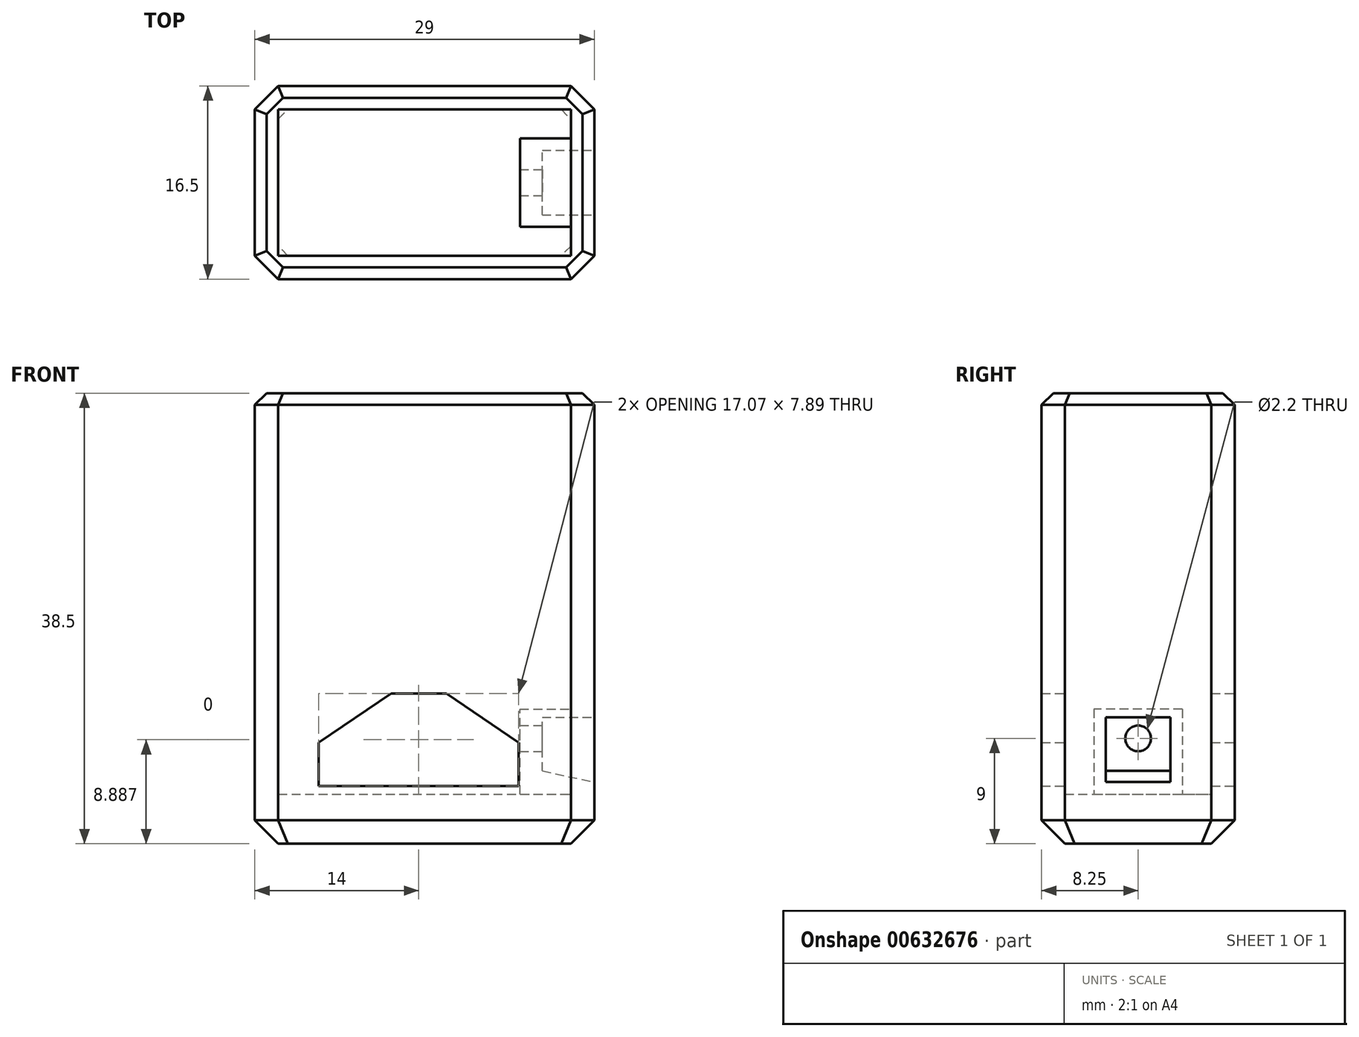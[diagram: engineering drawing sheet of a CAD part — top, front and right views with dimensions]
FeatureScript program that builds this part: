
annotation { "Feature Type Name" : "Feature", "Feature Type Description" : "" }
export const myFeature = defineFeature(function(context is Context, id is Id, definition is map)
    precondition{}
    {
        {
            var Q0;
            Q0=qCreatedBy(makeId("Top.planeOp"),FACE);
            var sketch = newSketch(context, id + "F0", { "sketchPlane" : qUnion([Q0])});
            skLineSegment(sketch, "E0.bottom", {"start": v(0, 0) * mm, "end": v(29, 0) * mm});
            skLineSegment(sketch, "E0.top", {"start": v(0, 16.5) * mm, "end": v(29, 16.5) * mm});
            skLineSegment(sketch, "E0.left", {"start": v(0, 0) * mm, "end": v(0, 16.5) * mm});
            skLineSegment(sketch, "E0.right", {"start": v(29, 0) * mm, "end": v(29, 16.5) * mm});
            skSolve(sketch);
        }
        {
            var Q0;
            Q0=makeQuery(id+"F0.imprint","IMPRINT",FACE,{"disambiguationData":[TD([[makeQuery(id+"F0.imprint","IMPRINT",EDGE,{"derivedFrom":sQuery(id+"F0.wireOp",EDGE,"E0.bottom")}),1.0]])]});
            extrude(context, id + "F1", {"entities" : qUnion([Q0]), "depth" : 38.5 * mm, "offsetDistance" : 25 * mm});
        }
        {
            var Q0;
            Q0=makeQuery(id+"F1.opExtrude","CAP_FACE",FACE,{"disambiguationData":[OSD([sQuery(id+"F0.wireOp",EDGE,"E0.bottom"),sQuery(id+"F0.wireOp",EDGE,"E0.top"),sQuery(id+"F0.wireOp",EDGE,"E0.left"),sQuery(id+"F0.wireOp",EDGE,"E0.right")])],"isStart":false});
            shell(context, id + "F2", {"entities" : qUnion([Q0]), "thickness" : 2 * mm});
        }
        {
            var Q0;
            Q0=makeQuery(id+"F2.opShell","OFFSET_FACE",FACE,{"disambiguationData":[OSD([sQuery(id+"F0.wireOp",EDGE,"E0.bottom"),sQuery(id+"F0.wireOp",EDGE,"E0.top"),sQuery(id+"F0.wireOp",EDGE,"E0.left"),sQuery(id+"F0.wireOp",EDGE,"E0.right")])]});
            extrude(context, id + "F3", {"entities" : qUnion([Q0]), "operationType" : NewBodyOperationType.ADD, "depth" : 2.25 * mm, "offsetDistance" : 25 * mm});
        }
        {
            var Q0;
            Q0=makeQuery(id+"F1.opExtrude","SWEPT_EDGE",EDGE,{"disambiguationData":[OSD([sQuery(id+"F0.wireOp",EDGE,"E0.bottom"),sQuery(id+"F0.wireOp",EDGE,"E0.right")])]});
            var Q1;
            Q1=makeQuery(id+"F1.opExtrude","SWEPT_EDGE",EDGE,{"disambiguationData":[OSD([sQuery(id+"F0.wireOp",EDGE,"E0.top"),sQuery(id+"F0.wireOp",EDGE,"E0.right")])]});
            var Q2;
            Q2=makeQuery(id+"F1.opExtrude","SWEPT_EDGE",EDGE,{"disambiguationData":[OSD([sQuery(id+"F0.wireOp",EDGE,"E0.bottom"),sQuery(id+"F0.wireOp",EDGE,"E0.left")])]});
            var Q3;
            Q3=makeQuery(id+"F1.opExtrude","SWEPT_EDGE",EDGE,{"disambiguationData":[OSD([sQuery(id+"F0.wireOp",EDGE,"E0.top"),sQuery(id+"F0.wireOp",EDGE,"E0.left")])]});
            chamfer(context, id + "F4", {"entities" : qUnion([Q0, Q1, Q2, Q3]), "width" : 2 * mm, "tangentPropagation" : true});
        }
        {
            var Q0;
            Q0=makeQuery(id+"F1.opExtrude","CAP_FACE",FACE,{"disambiguationData":[OSD([sQuery(id+"F0.wireOp",EDGE,"E0.bottom"),sQuery(id+"F0.wireOp",EDGE,"E0.top"),sQuery(id+"F0.wireOp",EDGE,"E0.left"),sQuery(id+"F0.wireOp",EDGE,"E0.right")])],"isStart":true});
            chamfer(context, id + "F5", {"entities" : qUnion([Q0]), "width" : 2 * mm, "tangentPropagation" : true});
        }
        {
            var Q0;
            Q0=makeQuery(id+"F1.opExtrude","CAP_EDGE",EDGE,{"disambiguationData":[OSD([sQuery(id+"F0.wireOp",EDGE,"E0.right")])],"isStart":false});
            var Q1;
            {var subQ0=sQuery(id+"F0.wireOp",EDGE,"E0.right");var subQ1=sQuery(id+"F0.wireOp",EDGE,"E0.bottom");Q1=makeQuery(id+"F4.opChamfer","BLEND_EDGE",EDGE,{"blendedFrom":[makeQuery(id+"F1.opExtrude","SWEPT_EDGE",EDGE,{"disambiguationData":[OSD([subQ1,subQ0])]}),makeQuery(id+"F1.opExtrude","CAP_FACE",FACE,{"disambiguationData":[OSD([subQ1,sQuery(id+"F0.wireOp",EDGE,"E0.top"),sQuery(id+"F0.wireOp",EDGE,"E0.left"),subQ0])],"isStart":false})],"blendedInto":[makeQuery(id+"F1.opExtrude","CAP_FACE",FACE,{"disambiguationData":[OSD([subQ1,sQuery(id+"F0.wireOp",EDGE,"E0.top"),sQuery(id+"F0.wireOp",EDGE,"E0.left"),subQ0])],"isStart":false})]});}
            var Q2;
            Q2=makeQuery(id+"F1.opExtrude","CAP_EDGE",EDGE,{"disambiguationData":[OSD([sQuery(id+"F0.wireOp",EDGE,"E0.bottom")])],"isStart":false});
            var Q3;
            {var subQ0=sQuery(id+"F0.wireOp",EDGE,"E0.left");var subQ1=sQuery(id+"F0.wireOp",EDGE,"E0.bottom");Q3=makeQuery(id+"F4.opChamfer","BLEND_EDGE",EDGE,{"blendedFrom":[makeQuery(id+"F1.opExtrude","SWEPT_EDGE",EDGE,{"disambiguationData":[OSD([subQ1,subQ0])]}),makeQuery(id+"F1.opExtrude","CAP_FACE",FACE,{"disambiguationData":[OSD([subQ1,sQuery(id+"F0.wireOp",EDGE,"E0.top"),subQ0,sQuery(id+"F0.wireOp",EDGE,"E0.right")])],"isStart":false})],"blendedInto":[makeQuery(id+"F1.opExtrude","CAP_FACE",FACE,{"disambiguationData":[OSD([subQ1,sQuery(id+"F0.wireOp",EDGE,"E0.top"),subQ0,sQuery(id+"F0.wireOp",EDGE,"E0.right")])],"isStart":false})]});}
            var Q4;
            Q4=makeQuery(id+"F1.opExtrude","CAP_EDGE",EDGE,{"disambiguationData":[OSD([sQuery(id+"F0.wireOp",EDGE,"E0.left")])],"isStart":false});
            var Q5;
            {var subQ0=sQuery(id+"F0.wireOp",EDGE,"E0.left");var subQ1=sQuery(id+"F0.wireOp",EDGE,"E0.top");Q5=makeQuery(id+"F4.opChamfer","BLEND_EDGE",EDGE,{"blendedFrom":[makeQuery(id+"F1.opExtrude","SWEPT_EDGE",EDGE,{"disambiguationData":[OSD([subQ1,subQ0])]}),makeQuery(id+"F1.opExtrude","CAP_FACE",FACE,{"disambiguationData":[OSD([sQuery(id+"F0.wireOp",EDGE,"E0.bottom"),subQ1,subQ0,sQuery(id+"F0.wireOp",EDGE,"E0.right")])],"isStart":false})],"blendedInto":[makeQuery(id+"F1.opExtrude","CAP_FACE",FACE,{"disambiguationData":[OSD([sQuery(id+"F0.wireOp",EDGE,"E0.bottom"),subQ1,subQ0,sQuery(id+"F0.wireOp",EDGE,"E0.right")])],"isStart":false})]});}
            var Q6;
            Q6=makeQuery(id+"F1.opExtrude","CAP_EDGE",EDGE,{"disambiguationData":[OSD([sQuery(id+"F0.wireOp",EDGE,"E0.top")])],"isStart":false});
            var Q7;
            {var subQ0=sQuery(id+"F0.wireOp",EDGE,"E0.right");var subQ1=sQuery(id+"F0.wireOp",EDGE,"E0.top");Q7=makeQuery(id+"F4.opChamfer","BLEND_EDGE",EDGE,{"blendedFrom":[makeQuery(id+"F1.opExtrude","SWEPT_EDGE",EDGE,{"disambiguationData":[OSD([subQ1,subQ0])]}),makeQuery(id+"F1.opExtrude","CAP_FACE",FACE,{"disambiguationData":[OSD([sQuery(id+"F0.wireOp",EDGE,"E0.bottom"),subQ1,sQuery(id+"F0.wireOp",EDGE,"E0.left"),subQ0])],"isStart":false})],"blendedInto":[makeQuery(id+"F1.opExtrude","CAP_FACE",FACE,{"disambiguationData":[OSD([sQuery(id+"F0.wireOp",EDGE,"E0.bottom"),subQ1,sQuery(id+"F0.wireOp",EDGE,"E0.left"),subQ0])],"isStart":false})]});}
            chamfer(context, id + "F6", {"entities" : qUnion([Q0, Q1, Q2, Q3, Q4, Q5, Q6, Q7]), "width" : 1 * mm, "tangentPropagation" : true});
        }
        {
            var Q0;
            Q0=makeQuery(id+"F1.opExtrude","SWEPT_FACE",FACE,{"disambiguationData":[OSD([sQuery(id+"F0.wireOp",EDGE,"E0.top")])]});
            var sketch = newSketch(context, id + "F7", { "sketchPlane" : qUnion([Q0])});
            skLineSegment(sketch, "E1", {"start": v(-22.54, 4.94) * mm, "end": v(-5.46, 4.94) * mm});
            skLineSegment(sketch, "E2", {"start": v(-5.46, 4.94) * mm, "end": v(-5.46, 8.66) * mm});
            skLineSegment(sketch, "E3", {"start": v(-5.46, 8.66) * mm, "end": v(-11.64, 12.83) * mm});
            skLineSegment(sketch, "E4", {"start": v(-11.63, 12.83) * mm, "end": v(-16.37, 12.83) * mm});
            skLineSegment(sketch, "E5", {"start": v(-16.36, 12.83) * mm, "end": v(-22.54, 8.66) * mm});
            skLineSegment(sketch, "E6", {"start": v(-22.54, 8.66) * mm, "end": v(-22.54, 4.94) * mm});
            skSolve(sketch);
        }
        {
            var Q0;
            Q0=makeQuery(id+"F7.imprint","IMPRINT",FACE,{"disambiguationData":[TD([[makeQuery(id+"F7.imprint","IMPRINT",EDGE,{"derivedFrom":sQuery(id+"F7.wireOp",EDGE,"E1")}),1.0]])]});
            extrude(context, id + "F8", {"entities" : qUnion([Q0]), "operationType" : NewBodyOperationType.REMOVE, "endBound" : BoundingType.THROUGH_ALL, "oppositeDirection" : true, "depth" : 25 * mm, "offsetDistance" : 25 * mm});
        }
        {
            var Q0;
            Q0=makeQuery(id+"F1.opExtrude","SWEPT_FACE",FACE,{"disambiguationData":[OSD([sQuery(id+"F0.wireOp",EDGE,"E0.right")])]});
            var sketch = newSketch(context, id + "F9", { "sketchPlane" : qUnion([Q0])});
            skLineSegment(sketch, "E7.bottom", {"start": v(4.48, 4.25) * mm, "end": v(12.02, 4.25) * mm});
            skLineSegment(sketch, "E7.top", {"start": v(4.48, 11.5) * mm, "end": v(12.02, 11.5) * mm});
            skLineSegment(sketch, "E7.left", {"start": v(4.48, 4.25) * mm, "end": v(4.48, 11.5) * mm});
            skLineSegment(sketch, "E7.right", {"start": v(12.02, 4.25) * mm, "end": v(12.02, 11.5) * mm});
            skCircle(sketch, "E8", {"center": v(8.25, 9) * mm, "radius": 1.1 * mm});
            skSolve(sketch);
        }
        {
            var Q0;
            Q0=makeQuery(id+"F9.imprint","IMPRINT",FACE,{"disambiguationData":[TD([[makeQuery(id+"F9.imprint","IMPRINT",EDGE,{"derivedFrom":sQuery(id+"F9.wireOp",EDGE,"E7.bottom")}),1.0]])]});
            extrude(context, id + "F10", {"entities" : qUnion([Q0]), "operationType" : NewBodyOperationType.ADD, "oppositeDirection" : true, "depth" : 6.35 * mm, "offsetDistance" : 25 * mm});
        }
        {
            var Q0;
            Q0=makeQuery(id+"F1.opExtrude","SWEPT_FACE",FACE,{"disambiguationData":[OSD([sQuery(id+"F0.wireOp",EDGE,"E0.right")])]});
            var sketch = newSketch(context, id + "F11", { "sketchPlane" : qUnion([Q0])});
            skLineSegment(sketch, "E9.bottom", {"start": v(5.48, 5.27) * mm, "end": v(11.02, 5.27) * mm});
            skLineSegment(sketch, "E9.top", {"start": v(5.48, 10.8) * mm, "end": v(11.02, 10.8) * mm});
            skLineSegment(sketch, "E9.left", {"start": v(5.48, 5.27) * mm, "end": v(5.48, 10.8) * mm});
            skLineSegment(sketch, "E9.right", {"start": v(11.02, 5.27) * mm, "end": v(11.02, 10.8) * mm});
            skSolve(sketch);
        }
        {
            var Q0;
            Q0=makeQuery(id+"F11.imprint","IMPRINT",FACE,{"disambiguationData":[TD([[makeQuery(id+"F11.imprint","IMPRINT",EDGE,{"derivedFrom":sQuery(id+"F11.wireOp",EDGE,"E9.bottom")}),-1.0]])]});
            cPlane(context, id + "F12", {"entities" : qUnion([Q0]), "cplaneType" : CPlaneType.OFFSET, "offset" : 4.45 * mm, "oppositeDirection" : true, "width" : 150 * mm, "height" : 150 * mm});
        }
        {
            var Q0;
            Q0=qCreatedBy(id+"F12.planeOp",FACE);
            var sketch = newSketch(context, id + "F13", { "sketchPlane" : qUnion([Q0])});
            skLineSegment(sketch, "E10.bottom", {"start": v(5.48, 6.22) * mm, "end": v(11.02, 6.22) * mm});
            skLineSegment(sketch, "E10.top", {"start": v(5.48, 10.8) * mm, "end": v(11.02, 10.8) * mm});
            skLineSegment(sketch, "E10.left", {"start": v(5.48, 6.22) * mm, "end": v(5.48, 10.8) * mm});
            skLineSegment(sketch, "E10.right", {"start": v(11.02, 6.22) * mm, "end": v(11.02, 10.8) * mm});
            skSolve(sketch);
        }
        {
            var Q1;
            Q1 = qSketchRegion(id + "F13", true);
            var Q2;
            Q2 = qSketchRegion(id + "F11", true);
            loft(context, id + "F14", {"operationType" : NewBodyOperationType.REMOVE, "sheetProfilesArray" : [{ "sheetProfileEntities" : qUnion([Q1]) }, { "sheetProfileEntities" : qUnion([Q2]) }]});
        }
    });
